# Revit family: JC KONTAKTER JCK218 FI
name_source: partatom
category: Specialty Equipment
units: mm (PartAtom-declared; Revit-internal decimal feet)

## family parameters
Cut with Voids When Loaded = No
Enable Cutting in Views = Yes
Host = Face
Maintain Annotation Orientation = Yes
Part Type = Normal
Room Calculation Point = No
Round Connector Dimension = Use Diameter
Shared = No

## types (1)
- JCK218
    CE asiakirja = https://jckontakter.se
    Default Elevation = 800 mm  [stored 2.62467 ft]
    Description = Kyynärkytkin, valmistettu valkoiseksi anodisoidusta alumiinista, jossa on valkoiset muoviset päätykappaleet. Neljä merkintäviivaa painopinnassa osoittavat, mistä kytkintä tulee painaa oven avaamisen aktivoimiseksi. Varustettu kosteussuojatulla mikrokytkimellä, jonka suojausluokitus on IP67. Sopii käytettäväksi sekä sisä- että ulkotiloissa.
    Kansi = Aluminum ENAW 6060 (Valkoinen)
    Kotelo = Aluminum ENAW 6060
    Manufacturer = JC Kontakter
    Mikrokytkimien määrä = 1
    Mikrokytkin = Standar NO IP67
    Model = JCK218
    Nimellisestä nimellisvirrasta = 1mA/4 V DC
    Pienin nimellisvirta = 12V Resistiivinen 6A Induktiivinen L/R 5ms 6A, 24V Resistiivinen 6A Induktiivinen L/R 5ms 5A
    Päätypäät = POM Tenac C 4520 (Valkoinen)
    Tekniken tuotekortti = https://www.jckontakter.fi
    Tuotteen paino = 0.305 kg
    URL = https://www.jckontakter.fi
    Valmistusmaa = Ruotsi

note: [stored X ft] marks values corroborated as IEEE doubles in the binary element streams (Revit-internal decimal feet)

## geometry (parser evidence)
native form markers: Sweep x6
no freeform markers — native parametric forms only
